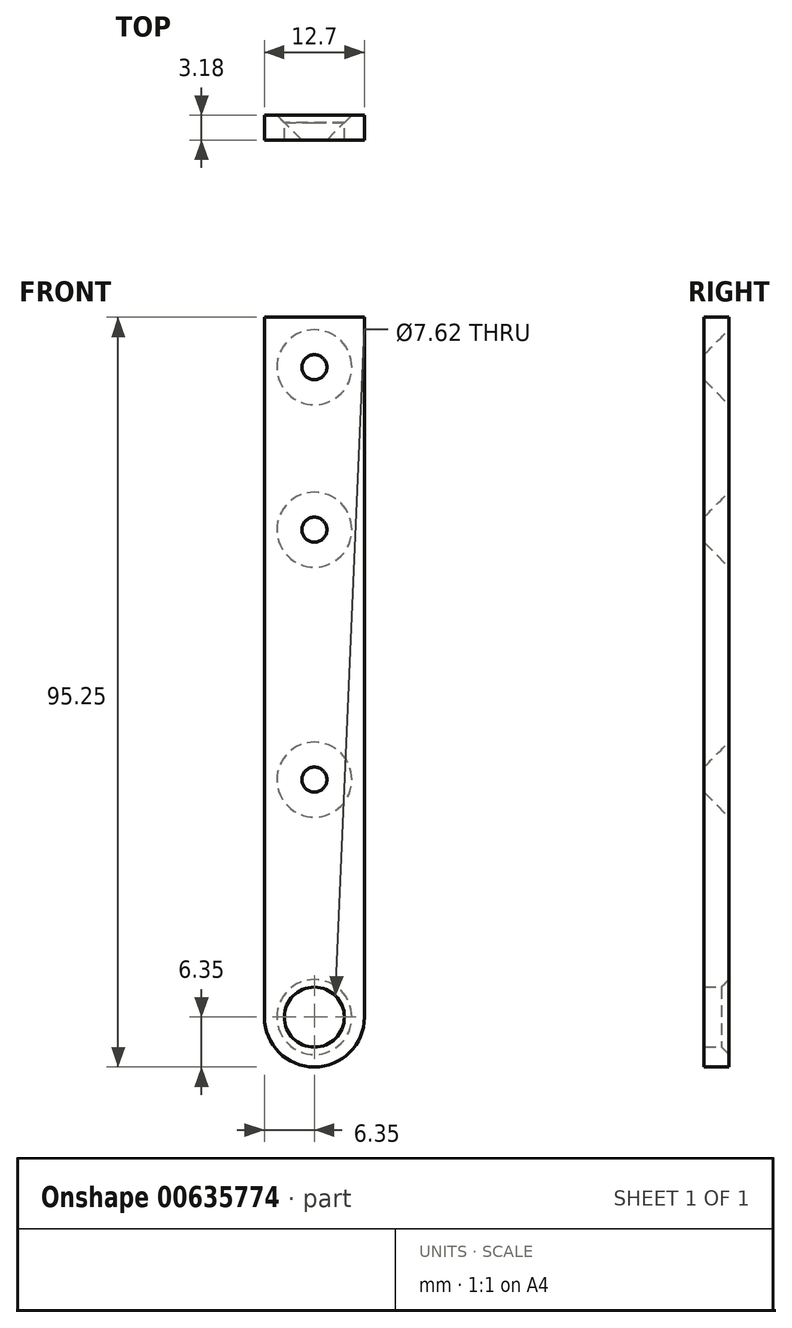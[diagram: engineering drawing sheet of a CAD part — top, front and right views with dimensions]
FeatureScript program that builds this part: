
annotation { "Feature Type Name" : "Feature", "Feature Type Description" : "" }
export const myFeature = defineFeature(function(context is Context, id is Id, definition is map)
    precondition{}
    {
        {
            var Q0;
            Q0=qCreatedBy(makeId("Front.planeOp"),FACE);
            var sketch = newSketch(context, id + "F0", { "sketchPlane" : qUnion([Q0])});
            skLineSegment(sketch, "E0.top", {"start": v(6.35, 88.9) * mm, "end": v(-6.35, 88.9) * mm});
            skLineSegment(sketch, "E0.left", {"start": v(6.35, 0) * mm, "end": v(6.35, 88.9) * mm});
            skLineSegment(sketch, "E0.right", {"start": v(-6.35, 0) * mm, "end": v(-6.35, 88.9) * mm});
            skPoint(sketch, "E1", {"position": v(0, 82.55) * mm});
            skPoint(sketch, "E2", {"position": v(0, 61.91) * mm});
            skArc(sketch, "E3", {"start": v(-6.35, 0) * mm, "mid": v(0, -6.35) * mm, "end": v(6.35, 0) * mm});
            skPoint(sketch, "E4", {"position": v(0, 30.16) * mm});
            skSolve(sketch);
        }
        {
            var Q0;
            Q0 = qSketchRegion(id + "F0", true);
            extrude(context, id + "F1", {"entities" : qUnion([Q0]), "depth" : 3.17 * mm, "offsetDistance" : 25.4 * mm});
        }
        {
            var Q0;
            Q0=sQuery(id+"F0.wireOp",VERTEX,"E1");
            var Q1;
            Q1=sQuery(id+"F0.wireOp",VERTEX,"E2");
            var Q2;
            Q2=sQuery(id+"F0.wireOp",VERTEX,"E4");
            var Q3;
            Q3=makeQuery(id+"F1.opExtrude","SWEPT_BODY",BODY,{"disambiguationData":[OSD([sQuery(id+"F0.wireOp",EDGE,"E0.top"),sQuery(id+"F0.wireOp",EDGE,"E0.left"),sQuery(id+"F0.wireOp",EDGE,"E0.right"),sQuery(id+"F0.wireOp",EDGE,"E3")])]});
            hole(context, id + "F2", {"style" : HoleStyle.C_SINK, "endStyle" : HoleEndStyle.THROUGH, "oppositeDirection" : true, "holeDiameter" : 2.54 * mm, "cSinkDiameter" : 9.52 * mm, "cSinkAngle" : 90 * degree, "majorDiameter" : 6.35 * mm, "isTappedThrough" : true, "tappedDepth" : 12.7 * mm, "tapClearance" : 3, "locations" : qUnion([Q0, Q1, Q2]), "scope" : qUnion([Q3])});
        }
        {
            var Q0;
            Q0=sQuery(id+"F0.wireOp",VERTEX,"E3.center");
            var Q1;
            Q1=makeQuery(id+"F1.opExtrude","SWEPT_BODY",BODY,{"disambiguationData":[OSD([sQuery(id+"F0.wireOp",EDGE,"E0.top"),sQuery(id+"F0.wireOp",EDGE,"E0.left"),sQuery(id+"F0.wireOp",EDGE,"E0.right"),sQuery(id+"F0.wireOp",EDGE,"E3")])]});
            hole(context, id + "F3", {"style" : HoleStyle.C_SINK, "endStyle" : HoleEndStyle.THROUGH, "oppositeDirection" : true, "holeDiameter" : 7.62 * mm, "cSinkDiameter" : 9.52 * mm, "cSinkAngle" : 90 * degree, "majorDiameter" : 6.35 * mm, "isTappedThrough" : true, "tappedDepth" : 12.7 * mm, "tapClearance" : 3, "locations" : qUnion([Q0]), "scope" : qUnion([Q1])});
        }
    });
